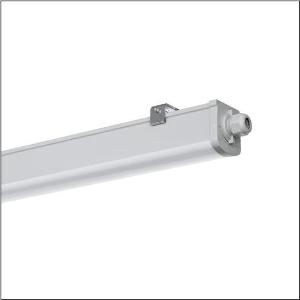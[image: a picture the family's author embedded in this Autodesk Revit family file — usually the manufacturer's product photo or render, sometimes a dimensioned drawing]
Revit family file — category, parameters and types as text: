
# Revit family: monsun_r__31_51fa207k450b_1d2e
name_source: partatom
category: Lighting Fixtures
units: mm (PartAtom-declared; Revit-internal decimal feet)

## family parameters
Cut with Voids When Loaded = No
Host = Face
Light Source = No
Part Type = Normal
Room Calculation Point = No
Round Connector Dimension = Use Diameter
Shared = No

## types (1)
- Monsun® 31 (1 x LED, 5100 lm, 38 W, 4000K)
    Apparent Load = 38 VA
    CIE Flux Codes = 42 72 91 92 100
    Color Rendering = 80
    Color Temperature = 4000K
    Default Elevation = 1800 mm
    Description = Monsun® 31, damp-proof luminaire, primary optical cover: diffuser, of PC, frosted, light emission: direct distribution, primary light characteristic: symmetric, installation type: surface-mounted, LED, rated luminous flux: 5.100lm, luminous efficacy: 134lm/W, light colour: 840, colour temperature: 4000K, control gear: ECG, with terminal, 3+1-pole, max. 2.5mm², through-wiring: 3x 2.5mm² + 1x 1.5mm², mains connection: 220..240V, AC, 50/60Hz, rated input power: 38W, housing, luminaire housing, of PC, light grey (RAL 7035), length: 1.158mm, width: 68mm, height: 76mm, protection rating (complete): IP66, insulation class (complete): insulation class II (safety insulation), certification: CE, ENEC, UKCA, protection symbol: D, impact resistance: IK08, permissible operating ambient temperature: -20..+40°C, corresponds to IFS (International Featured Standards) requirements for safety and quality in the food industry, contact your sales advisor before using the luminaires in applications with unclear chemical exposure, large temperature fluctuations or condensation-forming humidity, packaging unit: 1 piece
    Height = 77 mm
    Lamp = 1 x LED
    Lamp Light Flux = 5100 lm
    Lamp Power = 38 W
    Lamp count = 1
    Length = 1218 mm
    Luminous efficacy = 134 lm/W
    Manufacturer = Siteco
    ModVariant = No
    Model = 51FA207K450B
    Mounting Place = Ceiling
    Mounting Type = Surface mounted
    Number of Poles = 1
    OnlyDefault = Yes
    Power Factor = 1
    Product Name = Monsun® 31
    Product group = damp-proof luminaire
    ProductGroupID = 301
    Protection Class = Protection class II
    Protection Degree = IP 66
    RLX_Detail_Level = 1
    RLX_Emergency_Light_Flux = 0 lm
    RLX_Emergency_Type = 0
    RLX_Emergency_Type_DB = No
    RlxData = <blob elided: 32993 chars, md5=2e727d6b>
    Socket = socket
    Standby Power = 0 W
    System Light Flux = 5100 lm
    System Power = 38 W
    Type Comments = Product without accessories
    Type Image = l_1006174.jpg
    URL = http://relux.com
    VarID = ---
    Voltage = 0 V
    Weight = 0.00 kg
    Width = 69 mm

## geometry (parser evidence)
native form markers: Blend x4, Sweep x13
no freeform markers — native parametric forms only
